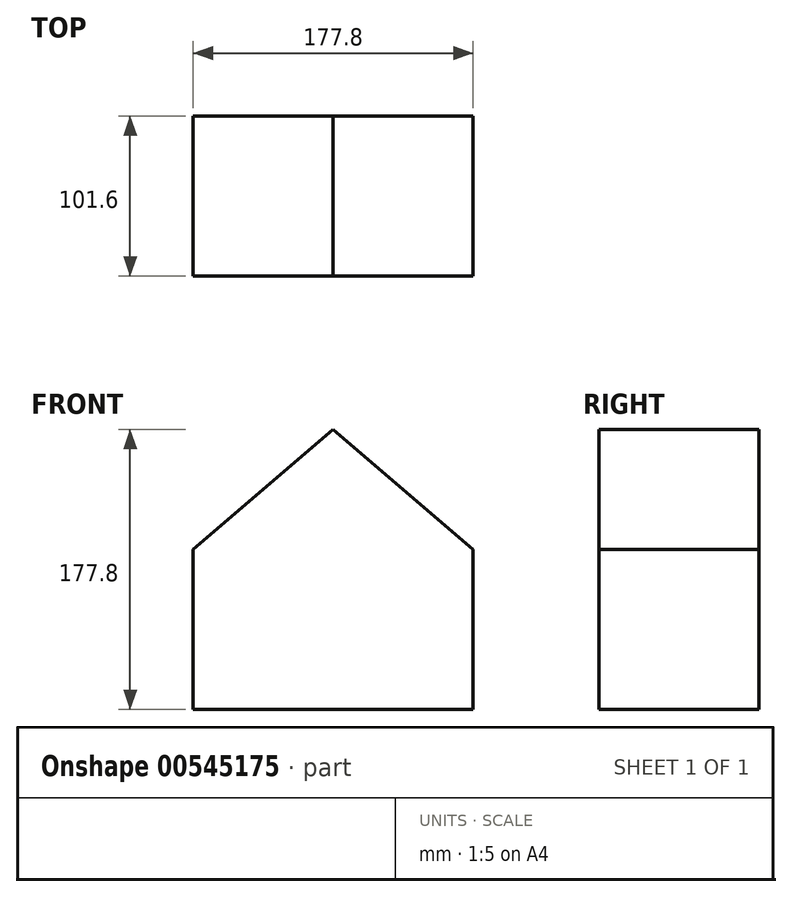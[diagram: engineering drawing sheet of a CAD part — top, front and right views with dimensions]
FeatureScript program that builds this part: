
annotation { "Feature Type Name" : "Feature", "Feature Type Description" : "" }
export const myFeature = defineFeature(function(context is Context, id is Id, definition is map)
    precondition{}
    {
        {
            var Q0;
            Q0=qCreatedBy(makeId("Front.planeOp"),FACE);
            var sketch = newSketch(context, id + "F0", { "sketchPlane" : qUnion([Q0])});
            skLineSegment(sketch, "E0.bottom", {"start": v(-88.9, 0) * mm, "end": v(88.9, 0) * mm});
            skLineSegment(sketch, "E0.top", {"start": v(-88.9, -101.6) * mm, "end": v(88.9, -101.6) * mm});
            skLineSegment(sketch, "E0.left", {"start": v(-88.9, 0) * mm, "end": v(-88.9, -101.6) * mm});
            skLineSegment(sketch, "E0.right", {"start": v(88.9, 0) * mm, "end": v(88.9, -101.6) * mm});
            skPoint(sketch, "E0.middle", {"position": v(0, -50.8) * mm});
            skSolve(sketch);
        }
        {
            var Q0;
            Q0 = qSketchRegion(id + "F0", true);
            extrude(context, id + "F1", {"entities" : qUnion([Q0]), "depth" : 101.6 * mm, "offsetDistance" : 25.4 * mm});
        }
        {
            var Q0;
            Q0=makeQuery(id+"F1.opExtrude","CAP_FACE",FACE,{"disambiguationData":[OSD([sQuery(id+"F0.wireOp",EDGE,"E0.bottom"),sQuery(id+"F0.wireOp",EDGE,"E0.top"),sQuery(id+"F0.wireOp",EDGE,"E0.left"),sQuery(id+"F0.wireOp",EDGE,"E0.right")])],"isStart":true});
            var sketch = newSketch(context, id + "F2", { "sketchPlane" : qUnion([Q0])});
            skLineSegment(sketch, "E1", {"start": v(88.9, 0) * mm, "end": v(0, 76.2) * mm});
            skLineSegment(sketch, "E2", {"start": v(-88.9, 0) * mm, "end": v(0, 76.2) * mm});
            skLineSegment(sketch, "E3", {"start": v(-88.9, 0) * mm, "end": v(88.9, 0) * mm});
            skSolve(sketch);
        }
        {
            var Q0;
            Q0 = qSketchRegion(id + "F2", true);
            var Q1;
            Q1=makeQuery(id+"F1.opExtrude","CAP_FACE",FACE,{"disambiguationData":[OSD([sQuery(id+"F0.wireOp",EDGE,"E0.bottom"),sQuery(id+"F0.wireOp",EDGE,"E0.top"),sQuery(id+"F0.wireOp",EDGE,"E0.left"),sQuery(id+"F0.wireOp",EDGE,"E0.right")])],"isStart":false});
            extrude(context, id + "F3", {"entities" : qUnion([Q0]), "operationType" : NewBodyOperationType.ADD, "endBound" : BoundingType.UP_TO_SURFACE, "oppositeDirection" : true, "depth" : 25.4 * mm, "endBoundEntityFace" : qUnion([Q1]), "offsetDistance" : 25.4 * mm});
        }
    });
